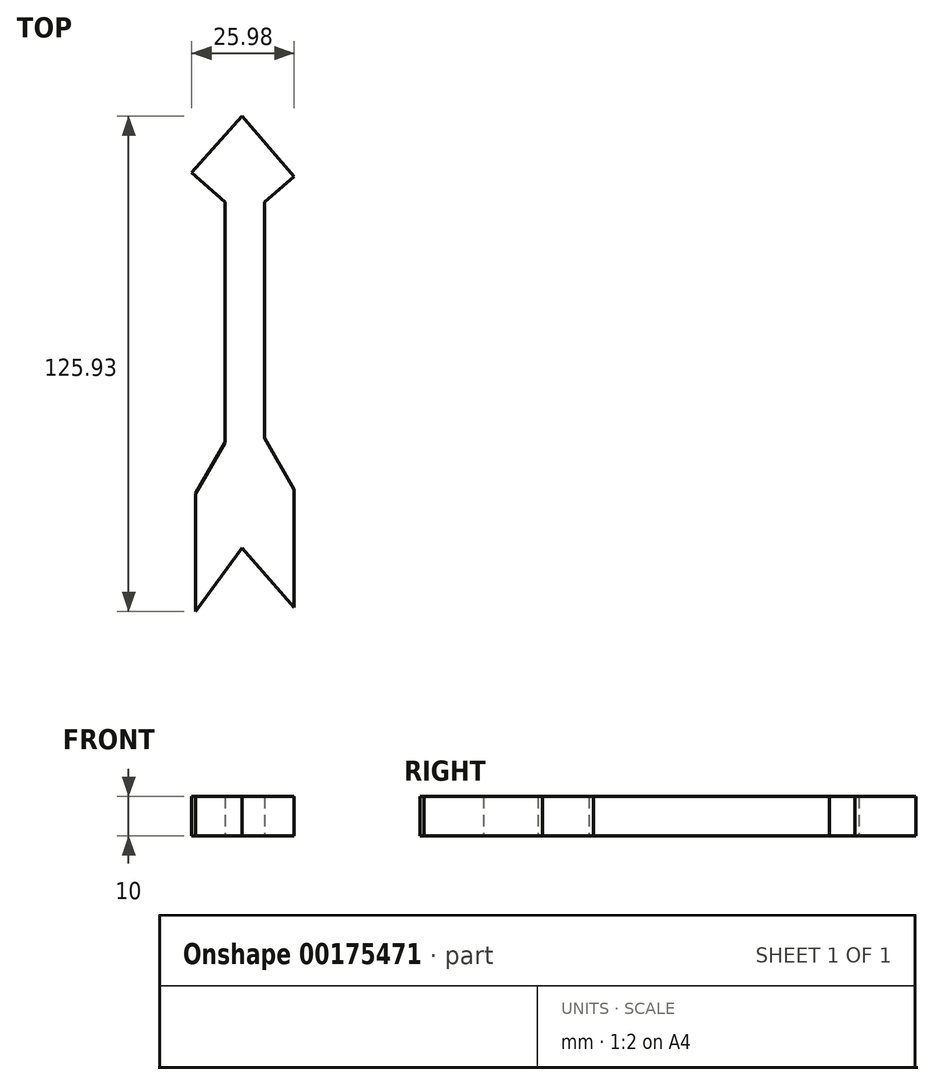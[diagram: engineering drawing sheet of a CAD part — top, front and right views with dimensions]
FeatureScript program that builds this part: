
annotation { "Feature Type Name" : "Feature", "Feature Type Description" : "" }
export const myFeature = defineFeature(function(context is Context, id is Id, definition is map)
    precondition{}
    {
        {
            var Q0;
            Q0=qCreatedBy(makeId("Top.planeOp"),FACE);
            var sketch = newSketch(context, id + "F0", { "sketchPlane" : qUnion([Q0])});
            skLineSegment(sketch, "E0", {"start": v(0, 69.8) * mm, "end": v(-12.76, 55.45) * mm});
            skLineSegment(sketch, "E1", {"start": v(13.22, 54.44) * mm, "end": v(0, 69.8) * mm});
            skLineSegment(sketch, "E2", {"start": v(-4.33, 47.95) * mm, "end": v(-4.33, -13.13) * mm});
            skLineSegment(sketch, "E3", {"start": v(5.67, -12.05) * mm, "end": v(5.67, 47.95) * mm});
            skLineSegment(sketch, "E4", {"start": v(-4.33, -13.13) * mm, "end": v(-11.83, -26.12) * mm});
            skLineSegment(sketch, "E5", {"start": v(-11.83, -26.12) * mm, "end": v(-11.83, -56.12) * mm});
            skLineSegment(sketch, "E6", {"start": v(-11.83, -56.12) * mm, "end": v(0, -40) * mm});
            skLineSegment(sketch, "E7", {"start": v(0, -40) * mm, "end": v(13.17, -55.04) * mm});
            skLineSegment(sketch, "E8", {"start": v(13.17, -55.04) * mm, "end": v(13.17, -25.04) * mm});
            skLineSegment(sketch, "E9", {"start": v(13.17, -25.04) * mm, "end": v(5.67, -12.05) * mm});
            skLineSegment(sketch, "E10", {"start": v(-4.33, 47.95) * mm, "end": v(-12.76, 55.45) * mm});
            skPoint(sketch, "E10.endSnap0", {"position": v(-12.76, 46.95) * mm});
            skPoint(sketch, "E11.start.orphan", {"position": v(-2.39, 52.43) * mm});
            skPoint(sketch, "E12.orphan", {"position": v(7.99, 49.4) * mm});
            skPoint(sketch, "E13.start.orphan", {"position": v(-21.2, 45.96) * mm});
            skLineSegment(sketch, "E14", {"start": v(5.67, 47.95) * mm, "end": v(13.22, 54.44) * mm});
            skPoint(sketch, "E15.orphan", {"position": v(18.8, 47.95) * mm});
            skSolve(sketch);
        }
        {
            var Q0;
            Q0=makeQuery(id+"F0.imprint","IMPRINT",FACE,{"disambiguationData":[TD([[makeQuery(id+"F0.imprint","IMPRINT",EDGE,{"derivedFrom":sQuery(id+"F0.wireOp",EDGE,"E0")}),1.0]])]});
            extrude(context, id + "F1", {"entities" : qUnion([Q0]), "depth" : 10 * mm});
        }
    });
